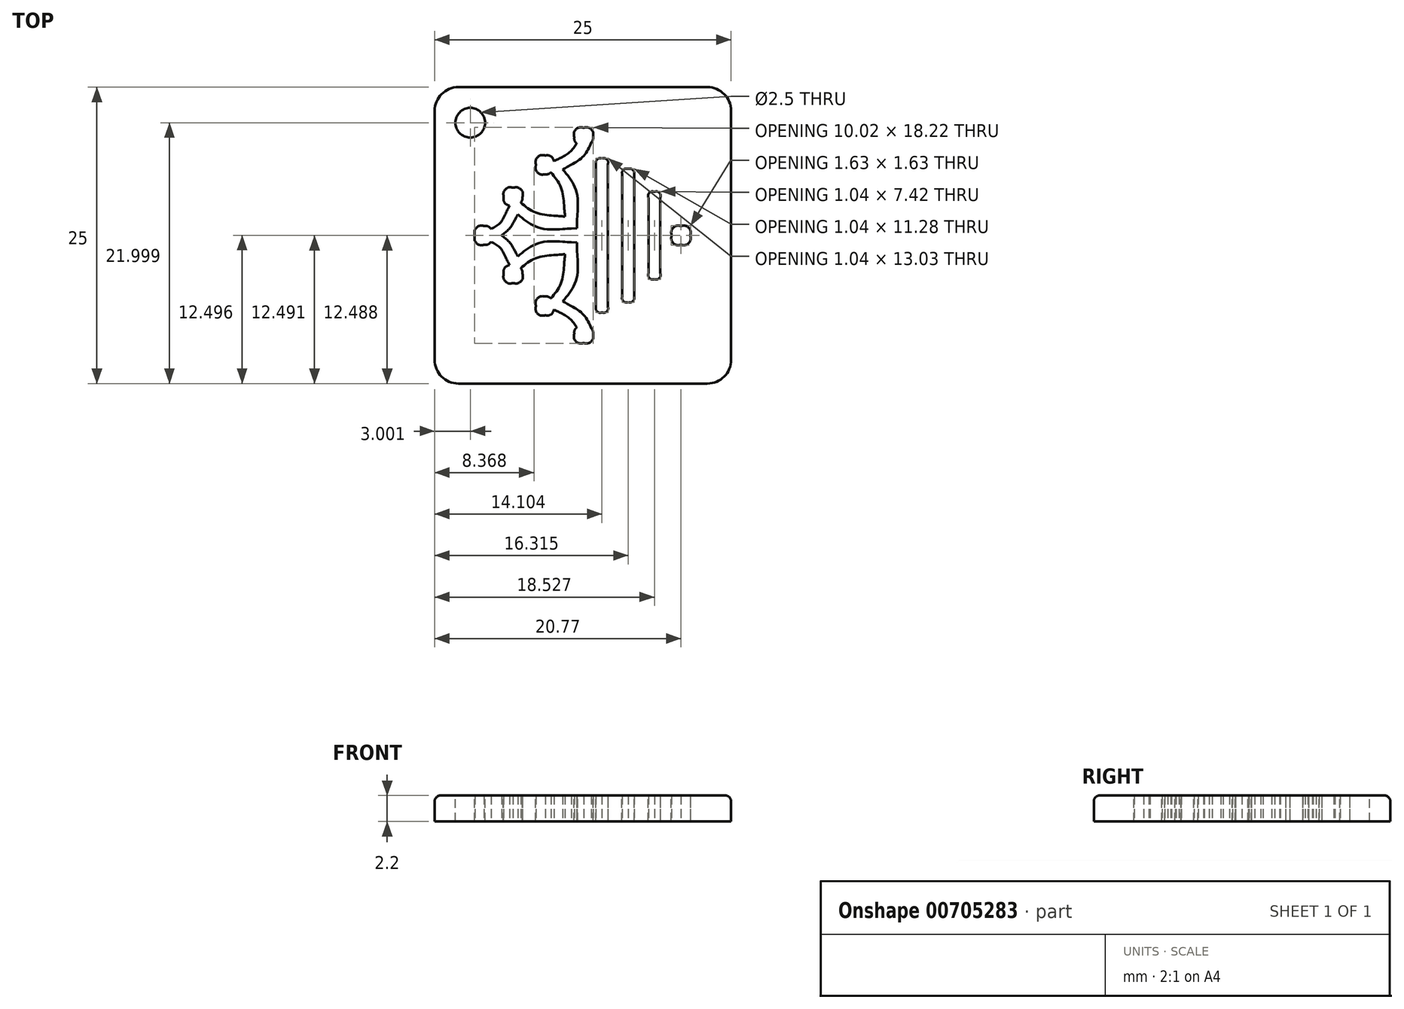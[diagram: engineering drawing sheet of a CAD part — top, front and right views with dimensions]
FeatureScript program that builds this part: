
annotation { "Feature Type Name" : "Feature", "Feature Type Description" : "" }
export const myFeature = defineFeature(function(context is Context, id is Id, definition is map)
    precondition{}
    {
        {
            var Q0;
            Q0=qCreatedBy(makeId("Top.planeOp"),FACE);
            var sketch = newSketch(context, id + "F0", { "sketchPlane" : qUnion([Q0])});
            skLineSegment(sketch, "E0", {"start": v(-141.73, -141.73) * mm, "end": v(141.73, -141.73) * mm});
            skLineSegment(sketch, "E1", {"start": v(141.73, -141.73) * mm, "end": v(141.73, 141.73) * mm});
            skLineSegment(sketch, "E2", {"start": v(141.73, 141.73) * mm, "end": v(-141.73, 141.73) * mm});
            skLineSegment(sketch, "E3", {"start": v(-141.73, 141.73) * mm, "end": v(-141.73, -141.73) * mm});
            skFitSpline(sketch, "E4", {"points": [v(18.18, 73.55) * mm, v(15.03, 73.55) * mm, v(12.48, 71) * mm, v(12.48, 67.84) * mm]});
            skLineSegment(sketch, "E5", {"start": v(12.48, 67.84) * mm, "end": v(12.48, -68.12) * mm});
            skFitSpline(sketch, "E6", {"points": [v(12.48, -68.12) * mm, v(12.48, -71.27) * mm, v(15.03, -73.82) * mm, v(18.18, -73.82) * mm]});
            skFitSpline(sketch, "E7", {"points": [v(18.18, -73.82) * mm, v(21.33, -73.82) * mm, v(23.89, -71.27) * mm, v(23.89, -68.12) * mm]});
            skLineSegment(sketch, "E8", {"start": v(23.89, -68.12) * mm, "end": v(23.89, 67.84) * mm});
            skFitSpline(sketch, "E9", {"points": [v(23.89, 67.84) * mm, v(23.89, 71) * mm, v(21.33, 73.55) * mm, v(18.18, 73.55) * mm]});
            skFitSpline(sketch, "E10", {"points": [v(43.26, 63.62) * mm, v(40.1, 63.62) * mm, v(37.56, 61.06) * mm, v(37.56, 57.91) * mm]});
            skLineSegment(sketch, "E11", {"start": v(37.56, 57.91) * mm, "end": v(37.56, -58.2) * mm});
            skFitSpline(sketch, "E12", {"points": [v(37.56, -58.2) * mm, v(37.56, -61.34) * mm, v(40.1, -63.9) * mm, v(43.26, -63.9) * mm]});
            skFitSpline(sketch, "E13", {"points": [v(43.26, -63.9) * mm, v(46.4, -63.9) * mm, v(48.96, -61.34) * mm, v(48.96, -58.2) * mm]});
            skLineSegment(sketch, "E14", {"start": v(48.96, -58.2) * mm, "end": v(48.96, 57.91) * mm});
            skFitSpline(sketch, "E15", {"points": [v(48.96, 57.91) * mm, v(48.96, 61.06) * mm, v(46.4, 63.62) * mm, v(43.26, 63.62) * mm]});
            skFitSpline(sketch, "E16", {"points": [v(68.34, 41.76) * mm, v(65.19, 41.76) * mm, v(62.63, 39.2) * mm, v(62.63, 36.05) * mm]});
            skLineSegment(sketch, "E17", {"start": v(62.63, 36.05) * mm, "end": v(62.63, -36.26) * mm});
            skFitSpline(sketch, "E18", {"points": [v(62.63, -36.26) * mm, v(62.63, -39.41) * mm, v(65.19, -41.97) * mm, v(68.34, -41.97) * mm]});
            skFitSpline(sketch, "E19", {"points": [v(68.34, -41.97) * mm, v(71.49, -41.97) * mm, v(74.04, -39.41) * mm, v(74.04, -36.26) * mm]});
            skLineSegment(sketch, "E20", {"start": v(74.04, -36.26) * mm, "end": v(74.04, 36.05) * mm});
            skFitSpline(sketch, "E21", {"points": [v(74.04, 36.05) * mm, v(74.04, 39.2) * mm, v(71.49, 41.76) * mm, v(68.34, 41.76) * mm]});
            skFitSpline(sketch, "E22", {"points": [v(93.78, 8.93) * mm, v(88.82, 8.93) * mm, v(84.8, 4.9) * mm, v(84.8, -0.05) * mm]});
            skFitSpline(sketch, "E23", {"points": [v(84.8, -0.05) * mm, v(84.8, -5) * mm, v(88.82, -9.03) * mm, v(93.78, -9.03) * mm]});
            skFitSpline(sketch, "E24", {"points": [v(93.78, -9.03) * mm, v(98.73, -9.03) * mm, v(102.75, -5) * mm, v(102.75, -0.05) * mm]});
            skFitSpline(sketch, "E25", {"points": [v(102.75, -0.05) * mm, v(102.75, 4.9) * mm, v(98.73, 8.93) * mm, v(93.78, 8.93) * mm]});
            skFitSpline(sketch, "E26", {"points": [v(7.97, 88.74) * mm, v(9.03, 90.21) * mm, v(9.66, 92.01) * mm, v(9.66, 93.97) * mm]});
            skFitSpline(sketch, "E27", {"points": [v(9.66, 93.97) * mm, v(9.66, 98.92) * mm, v(5.64, 102.94) * mm, v(0.69, 102.94) * mm]});
            skFitSpline(sketch, "E28", {"points": [v(0.69, 102.94) * mm, v(-4.27, 102.94) * mm, v(-8.28, 98.92) * mm, v(-8.28, 93.97) * mm]});
            skFitSpline(sketch, "E29", {"points": [v(-8.28, 93.97) * mm, v(-8.28, 91.64) * mm, v(-7.4, 89.54) * mm, v(-5.95, 87.94) * mm]});
            skFitSpline(sketch, "E30", {"points": [v(-5.95, 87.94) * mm, v(-13.68, 78.6) * mm, v(-23.82, 72.91) * mm, v(-27.73, 70.94) * mm]});
            skFitSpline(sketch, "E31", {"points": [v(-27.73, 70.94) * mm, v(-29.1, 74.14) * mm, v(-32.28, 76.38) * mm, v(-35.98, 76.38) * mm]});
            skFitSpline(sketch, "E32", {"points": [v(-35.98, 76.38) * mm, v(-40.93, 76.38) * mm, v(-44.95, 72.36) * mm, v(-44.95, 67.4) * mm]});
            skFitSpline(sketch, "E33", {"points": [v(-44.95, 67.4) * mm, v(-44.95, 62.44) * mm, v(-40.93, 58.42) * mm, v(-35.98, 58.42) * mm]});
            skFitSpline(sketch, "E34", {"points": [v(-35.98, 58.42) * mm, v(-33.95, 58.42) * mm, v(-32.09, 59.1) * mm, v(-30.58, 60.24) * mm]});
            skFitSpline(sketch, "E35", {"points": [v(-30.58, 60.24) * mm, v(-20.67, 44.96) * mm, v(-17.87, 26.91) * mm, v(-17.08, 17.88) * mm]});
            skFitSpline(sketch, "E36", {"points": [v(-17.08, 17.88) * mm, v(-26.13, 18.65) * mm, v(-44.2, 21.44) * mm, v(-59.47, 31.37) * mm]});
            skFitSpline(sketch, "E37", {"points": [v(-59.47, 31.37) * mm, v(-58.4, 32.85) * mm, v(-57.76, 34.66) * mm, v(-57.76, 36.63) * mm]});
            skFitSpline(sketch, "E38", {"points": [v(-57.76, 36.63) * mm, v(-57.76, 41.6) * mm, v(-61.77, 45.61) * mm, v(-66.73, 45.61) * mm]});
            skFitSpline(sketch, "E39", {"points": [v(-66.73, 45.61) * mm, v(-71.68, 45.61) * mm, v(-75.7, 41.6) * mm, v(-75.7, 36.63) * mm]});
            skFitSpline(sketch, "E40", {"points": [v(-75.7, 36.63) * mm, v(-75.7, 32.9) * mm, v(-73.43, 29.71) * mm, v(-70.2, 28.35) * mm]});
            skFitSpline(sketch, "E41", {"points": [v(-70.2, 28.35) * mm, v(-72.44, 23.85) * mm, v(-78.89, 12.16) * mm, v(-87.87, 6.09) * mm]});
            skFitSpline(sketch, "E42", {"points": [v(-87.87, 6.09) * mm, v(-89.5, 7.83) * mm, v(-91.82, 8.93) * mm, v(-94.4, 8.93) * mm]});
            skFitSpline(sketch, "E43", {"points": [v(-94.4, 8.93) * mm, v(-99.36, 8.93) * mm, v(-103.38, 4.9) * mm, v(-103.38, -0.05) * mm]});
            skFitSpline(sketch, "E44", {"points": [v(-103.38, -0.05) * mm, v(-103.38, -5) * mm, v(-99.36, -9.03) * mm, v(-94.4, -9.03) * mm]});
            skFitSpline(sketch, "E45", {"points": [v(-94.4, -9.03) * mm, v(-91.82, -9.03) * mm, v(-89.49, -7.92) * mm, v(-87.85, -6.17) * mm]});
            skFitSpline(sketch, "E46", {"points": [v(-87.85, -6.17) * mm, v(-78.88, -12.25) * mm, v(-72.44, -23.95) * mm, v(-70.2, -28.45) * mm]});
            skFitSpline(sketch, "E47", {"points": [v(-70.2, -28.45) * mm, v(-73.43, -29.8) * mm, v(-75.7, -33) * mm, v(-75.7, -36.73) * mm]});
            skFitSpline(sketch, "E48", {"points": [v(-75.7, -36.73) * mm, v(-75.7, -41.69) * mm, v(-71.68, -45.7) * mm, v(-66.73, -45.7) * mm]});
            skFitSpline(sketch, "E49", {"points": [v(-66.73, -45.7) * mm, v(-61.77, -45.7) * mm, v(-57.76, -41.69) * mm, v(-57.76, -36.73) * mm]});
            skFitSpline(sketch, "E50", {"points": [v(-57.76, -36.73) * mm, v(-57.76, -34.76) * mm, v(-58.4, -32.95) * mm, v(-59.47, -31.47) * mm]});
            skFitSpline(sketch, "E51", {"points": [v(-59.47, -31.47) * mm, v(-44.2, -21.53) * mm, v(-26.11, -18.75) * mm, v(-17.07, -17.97) * mm]});
            skFitSpline(sketch, "E52", {"points": [v(-17.07, -17.97) * mm, v(-17.85, -27) * mm, v(-20.63, -45) * mm, v(-30.58, -60.34) * mm]});
            skFitSpline(sketch, "E53", {"points": [v(-30.58, -60.34) * mm, v(-32.09, -59.2) * mm, v(-33.95, -58.52) * mm, v(-35.98, -58.52) * mm]});
            skFitSpline(sketch, "E54", {"points": [v(-35.98, -58.52) * mm, v(-40.93, -58.52) * mm, v(-44.95, -62.54) * mm, v(-44.95, -67.5) * mm]});
            skFitSpline(sketch, "E55", {"points": [v(-44.95, -67.5) * mm, v(-44.95, -72.45) * mm, v(-40.93, -76.47) * mm, v(-35.98, -76.47) * mm]});
            skFitSpline(sketch, "E56", {"points": [v(-35.98, -76.47) * mm, v(-32.28, -76.47) * mm, v(-29.1, -74.23) * mm, v(-27.73, -71.03) * mm]});
            skFitSpline(sketch, "E57", {"points": [v(-27.73, -71.03) * mm, v(-23.81, -72.99) * mm, v(-13.69, -78.64) * mm, v(-5.95, -88.03) * mm]});
            skFitSpline(sketch, "E58", {"points": [v(-5.95, -88.03) * mm, v(-7.4, -89.63) * mm, v(-8.28, -91.74) * mm, v(-8.28, -94.06) * mm]});
            skFitSpline(sketch, "E59", {"points": [v(-8.28, -94.06) * mm, v(-8.28, -99.02) * mm, v(-4.27, -103.04) * mm, v(0.69, -103.04) * mm]});
            skFitSpline(sketch, "E60", {"points": [v(0.69, -103.04) * mm, v(5.64, -103.04) * mm, v(9.66, -99.02) * mm, v(9.66, -94.06) * mm]});
            skFitSpline(sketch, "E61", {"points": [v(9.66, -94.06) * mm, v(9.66, -92.11) * mm, v(9.03, -90.31) * mm, v(7.97, -88.84) * mm]});
            skFitSpline(sketch, "E62", {"points": [v(7.97, -88.84) * mm, v(0.27, -75.6) * mm, v(-12.12, -67.14) * mm, v(-19.34, -63.05) * mm]});
            skFitSpline(sketch, "E63", {"points": [v(-19.34, -63.05) * mm, v(-5.74, -39.72) * mm, v(-5.77, -13.33) * mm, v(-5.78, -12.13) * mm]});
            skLineSegment(sketch, "E64", {"start": v(-5.78, -12.13) * mm, "end": v(-5.82, -6.73) * mm});
            skLineSegment(sketch, "E65", {"start": v(-5.82, -6.73) * mm, "end": v(-11.23, -6.68) * mm});
            skFitSpline(sketch, "E66", {"points": [v(-11.23, -6.68) * mm, v(-12.42, -6.66) * mm, v(-38.8, -6.6) * mm, v(-62.12, -20.18) * mm]});
            skFitSpline(sketch, "E67", {"points": [v(-62.12, -20.18) * mm, v(-65.16, -14.68) * mm, v(-70.52, -6.3) * mm, v(-77.82, -0.04) * mm]});
            skFitSpline(sketch, "E68", {"points": [v(-77.82, -0.04) * mm, v(-70.53, 6.22) * mm, v(-65.16, 14.6) * mm, v(-62.12, 20.09) * mm]});
            skFitSpline(sketch, "E69", {"points": [v(-62.12, 20.09) * mm, v(-38.81, 6.5) * mm, v(-12.43, 6.56) * mm, v(-11.23, 6.58) * mm]});
            skLineSegment(sketch, "E70", {"start": v(-11.23, 6.58) * mm, "end": v(-5.82, 6.63) * mm});
            skLineSegment(sketch, "E71", {"start": v(-5.82, 6.63) * mm, "end": v(-5.78, 12.04) * mm});
            skFitSpline(sketch, "E72", {"points": [v(-5.78, 12.04) * mm, v(-5.77, 13.23) * mm, v(-5.75, 39.63) * mm, v(-19.34, 62.95) * mm]});
            skFitSpline(sketch, "E73", {"points": [v(-19.34, 62.95) * mm, v(-12.12, 67.04) * mm, v(0.27, 75.5) * mm, v(7.97, 88.74) * mm]});
            skSolve(sketch);
        }
        {
            var Q0;
            Q0=makeQuery(id+"F0.imprint","IMPRINT",FACE,{"disambiguationData":[TD([[makeQuery(id+"F0.imprint","IMPRINT",EDGE,{"derivedFrom":sQuery(id+"F0.wireOp",EDGE,"E0")}),1.0]])]});
            extrude(context, id + "F1", {"entities" : qUnion([Q0]), "depth" : 25 * mm, "offsetDistance" : 25 * mm});
        }
        {
            var Q0;
            Q0=makeQuery(id+"F1.opExtrude","SWEPT_BODY",BODY,{"disambiguationData":[OSD([sQuery(id+"F0.wireOp",EDGE,"E0"),sQuery(id+"F0.wireOp",EDGE,"E1"),sQuery(id+"F0.wireOp",EDGE,"E2"),sQuery(id+"F0.wireOp",EDGE,"E3"),sQuery(id+"F0.wireOp",EDGE,"E4"),sQuery(id+"F0.wireOp",EDGE,"E5"),sQuery(id+"F0.wireOp",EDGE,"E6"),sQuery(id+"F0.wireOp",EDGE,"E7"),sQuery(id+"F0.wireOp",EDGE,"E8"),sQuery(id+"F0.wireOp",EDGE,"E9"),sQuery(id+"F0.wireOp",EDGE,"E10"),sQuery(id+"F0.wireOp",EDGE,"E11"),sQuery(id+"F0.wireOp",EDGE,"E12"),sQuery(id+"F0.wireOp",EDGE,"E13"),sQuery(id+"F0.wireOp",EDGE,"E14"),sQuery(id+"F0.wireOp",EDGE,"E15"),sQuery(id+"F0.wireOp",EDGE,"E16"),sQuery(id+"F0.wireOp",EDGE,"E17"),sQuery(id+"F0.wireOp",EDGE,"E18"),sQuery(id+"F0.wireOp",EDGE,"E19"),sQuery(id+"F0.wireOp",EDGE,"E20"),sQuery(id+"F0.wireOp",EDGE,"E21"),sQuery(id+"F0.wireOp",EDGE,"E22"),sQuery(id+"F0.wireOp",EDGE,"E23"),sQuery(id+"F0.wireOp",EDGE,"E24"),sQuery(id+"F0.wireOp",EDGE,"E25"),sQuery(id+"F0.wireOp",EDGE,"E26"),sQuery(id+"F0.wireOp",EDGE,"E27"),sQuery(id+"F0.wireOp",EDGE,"E28"),sQuery(id+"F0.wireOp",EDGE,"E29"),sQuery(id+"F0.wireOp",EDGE,"E30"),sQuery(id+"F0.wireOp",EDGE,"E31"),sQuery(id+"F0.wireOp",EDGE,"E32"),sQuery(id+"F0.wireOp",EDGE,"E33"),sQuery(id+"F0.wireOp",EDGE,"E34"),sQuery(id+"F0.wireOp",EDGE,"E35"),sQuery(id+"F0.wireOp",EDGE,"E36"),sQuery(id+"F0.wireOp",EDGE,"E37"),sQuery(id+"F0.wireOp",EDGE,"E38"),sQuery(id+"F0.wireOp",EDGE,"E39"),sQuery(id+"F0.wireOp",EDGE,"E40"),sQuery(id+"F0.wireOp",EDGE,"E41"),sQuery(id+"F0.wireOp",EDGE,"E42"),sQuery(id+"F0.wireOp",EDGE,"E43"),sQuery(id+"F0.wireOp",EDGE,"E44"),sQuery(id+"F0.wireOp",EDGE,"E45"),sQuery(id+"F0.wireOp",EDGE,"E46"),sQuery(id+"F0.wireOp",EDGE,"E47"),sQuery(id+"F0.wireOp",EDGE,"E48"),sQuery(id+"F0.wireOp",EDGE,"E49"),sQuery(id+"F0.wireOp",EDGE,"E50"),sQuery(id+"F0.wireOp",EDGE,"E51"),sQuery(id+"F0.wireOp",EDGE,"E52"),sQuery(id+"F0.wireOp",EDGE,"E53"),sQuery(id+"F0.wireOp",EDGE,"E54"),sQuery(id+"F0.wireOp",EDGE,"E55"),sQuery(id+"F0.wireOp",EDGE,"E56"),sQuery(id+"F0.wireOp",EDGE,"E57"),sQuery(id+"F0.wireOp",EDGE,"E58"),sQuery(id+"F0.wireOp",EDGE,"E59"),sQuery(id+"F0.wireOp",EDGE,"E60"),sQuery(id+"F0.wireOp",EDGE,"E61"),sQuery(id+"F0.wireOp",EDGE,"E62"),sQuery(id+"F0.wireOp",EDGE,"E63"),sQuery(id+"F0.wireOp",EDGE,"E64"),sQuery(id+"F0.wireOp",EDGE,"E65"),sQuery(id+"F0.wireOp",EDGE,"E66"),sQuery(id+"F0.wireOp",EDGE,"E67"),sQuery(id+"F0.wireOp",EDGE,"E68"),sQuery(id+"F0.wireOp",EDGE,"E69"),sQuery(id+"F0.wireOp",EDGE,"E70"),sQuery(id+"F0.wireOp",EDGE,"E71"),sQuery(id+"F0.wireOp",EDGE,"E72"),sQuery(id+"F0.wireOp",EDGE,"E73")])]});
            var Q1;
            Q1=qCreatedBy(makeId("Origin.pointOp"),VERTEX);
            transform(context, id + "F2", {"entities" : qUnion([Q0]), "transformType" : TransformType.SCALE_UNIFORMLY, "scale" : 0.35 / 4, "scalePoint" : qUnion([Q1]), "makeCopy" : false});
        }
        {
            var Q0;
            Q0=makeQuery(id+"F1.opExtrude","CAP_FACE",FACE,{"disambiguationData":[OSD([sQuery(id+"F0.wireOp",EDGE,"E0"),sQuery(id+"F0.wireOp",EDGE,"E1"),sQuery(id+"F0.wireOp",EDGE,"E2"),sQuery(id+"F0.wireOp",EDGE,"E3"),sQuery(id+"F0.wireOp",EDGE,"E4"),sQuery(id+"F0.wireOp",EDGE,"E5"),sQuery(id+"F0.wireOp",EDGE,"E6"),sQuery(id+"F0.wireOp",EDGE,"E7"),sQuery(id+"F0.wireOp",EDGE,"E8"),sQuery(id+"F0.wireOp",EDGE,"E9"),sQuery(id+"F0.wireOp",EDGE,"E10"),sQuery(id+"F0.wireOp",EDGE,"E11"),sQuery(id+"F0.wireOp",EDGE,"E12"),sQuery(id+"F0.wireOp",EDGE,"E13"),sQuery(id+"F0.wireOp",EDGE,"E14"),sQuery(id+"F0.wireOp",EDGE,"E15"),sQuery(id+"F0.wireOp",EDGE,"E16"),sQuery(id+"F0.wireOp",EDGE,"E17"),sQuery(id+"F0.wireOp",EDGE,"E18"),sQuery(id+"F0.wireOp",EDGE,"E19"),sQuery(id+"F0.wireOp",EDGE,"E20"),sQuery(id+"F0.wireOp",EDGE,"E21"),sQuery(id+"F0.wireOp",EDGE,"E22"),sQuery(id+"F0.wireOp",EDGE,"E23"),sQuery(id+"F0.wireOp",EDGE,"E24"),sQuery(id+"F0.wireOp",EDGE,"E25"),sQuery(id+"F0.wireOp",EDGE,"E26"),sQuery(id+"F0.wireOp",EDGE,"E27"),sQuery(id+"F0.wireOp",EDGE,"E28"),sQuery(id+"F0.wireOp",EDGE,"E29"),sQuery(id+"F0.wireOp",EDGE,"E30"),sQuery(id+"F0.wireOp",EDGE,"E31"),sQuery(id+"F0.wireOp",EDGE,"E32"),sQuery(id+"F0.wireOp",EDGE,"E33"),sQuery(id+"F0.wireOp",EDGE,"E34"),sQuery(id+"F0.wireOp",EDGE,"E35"),sQuery(id+"F0.wireOp",EDGE,"E36"),sQuery(id+"F0.wireOp",EDGE,"E37"),sQuery(id+"F0.wireOp",EDGE,"E38"),sQuery(id+"F0.wireOp",EDGE,"E39"),sQuery(id+"F0.wireOp",EDGE,"E40"),sQuery(id+"F0.wireOp",EDGE,"E41"),sQuery(id+"F0.wireOp",EDGE,"E42"),sQuery(id+"F0.wireOp",EDGE,"E43"),sQuery(id+"F0.wireOp",EDGE,"E44"),sQuery(id+"F0.wireOp",EDGE,"E45"),sQuery(id+"F0.wireOp",EDGE,"E46"),sQuery(id+"F0.wireOp",EDGE,"E47"),sQuery(id+"F0.wireOp",EDGE,"E48"),sQuery(id+"F0.wireOp",EDGE,"E49"),sQuery(id+"F0.wireOp",EDGE,"E50"),sQuery(id+"F0.wireOp",EDGE,"E51"),sQuery(id+"F0.wireOp",EDGE,"E52"),sQuery(id+"F0.wireOp",EDGE,"E53"),sQuery(id+"F0.wireOp",EDGE,"E54"),sQuery(id+"F0.wireOp",EDGE,"E55"),sQuery(id+"F0.wireOp",EDGE,"E56"),sQuery(id+"F0.wireOp",EDGE,"E57"),sQuery(id+"F0.wireOp",EDGE,"E58"),sQuery(id+"F0.wireOp",EDGE,"E59"),sQuery(id+"F0.wireOp",EDGE,"E60"),sQuery(id+"F0.wireOp",EDGE,"E61"),sQuery(id+"F0.wireOp",EDGE,"E62"),sQuery(id+"F0.wireOp",EDGE,"E63"),sQuery(id+"F0.wireOp",EDGE,"E64"),sQuery(id+"F0.wireOp",EDGE,"E65"),sQuery(id+"F0.wireOp",EDGE,"E66"),sQuery(id+"F0.wireOp",EDGE,"E67"),sQuery(id+"F0.wireOp",EDGE,"E68"),sQuery(id+"F0.wireOp",EDGE,"E69"),sQuery(id+"F0.wireOp",EDGE,"E70"),sQuery(id+"F0.wireOp",EDGE,"E71"),sQuery(id+"F0.wireOp",EDGE,"E72"),sQuery(id+"F0.wireOp",EDGE,"E73")])],"isStart":false});
            var sketch = newSketch(context, id + "F3", { "sketchPlane" : qUnion([Q0])});
            skLineSegment(sketch, "E74.0", {"start": v(12.5, 9.5) * mm, "end": v(-12.5, 9.5) * mm, "construction": true});
            skLineSegment(sketch, "E75.0", {"start": v(-9.5, 12.5) * mm, "end": v(-9.5, -12.5) * mm, "construction": true});
            skCircle(sketch, "E76", {"center": v(-9.5, 9.5) * mm, "radius": 1.33 * mm, "construction": true});
            skSolve(sketch);
        }
        {
            var Q0;
            Q0=sQuery(id+"F3.wireOp",VERTEX,"E76.center");
            var Q1;
            Q1=makeQuery(id+"F1.opExtrude","SWEPT_BODY",BODY,{"disambiguationData":[OSD([sQuery(id+"F0.wireOp",EDGE,"E0"),sQuery(id+"F0.wireOp",EDGE,"E1"),sQuery(id+"F0.wireOp",EDGE,"E2"),sQuery(id+"F0.wireOp",EDGE,"E3"),sQuery(id+"F0.wireOp",EDGE,"E4"),sQuery(id+"F0.wireOp",EDGE,"E5"),sQuery(id+"F0.wireOp",EDGE,"E6"),sQuery(id+"F0.wireOp",EDGE,"E7"),sQuery(id+"F0.wireOp",EDGE,"E8"),sQuery(id+"F0.wireOp",EDGE,"E9"),sQuery(id+"F0.wireOp",EDGE,"E10"),sQuery(id+"F0.wireOp",EDGE,"E11"),sQuery(id+"F0.wireOp",EDGE,"E12"),sQuery(id+"F0.wireOp",EDGE,"E13"),sQuery(id+"F0.wireOp",EDGE,"E14"),sQuery(id+"F0.wireOp",EDGE,"E15"),sQuery(id+"F0.wireOp",EDGE,"E16"),sQuery(id+"F0.wireOp",EDGE,"E17"),sQuery(id+"F0.wireOp",EDGE,"E18"),sQuery(id+"F0.wireOp",EDGE,"E19"),sQuery(id+"F0.wireOp",EDGE,"E20"),sQuery(id+"F0.wireOp",EDGE,"E21"),sQuery(id+"F0.wireOp",EDGE,"E22"),sQuery(id+"F0.wireOp",EDGE,"E23"),sQuery(id+"F0.wireOp",EDGE,"E24"),sQuery(id+"F0.wireOp",EDGE,"E25"),sQuery(id+"F0.wireOp",EDGE,"E26"),sQuery(id+"F0.wireOp",EDGE,"E27"),sQuery(id+"F0.wireOp",EDGE,"E28"),sQuery(id+"F0.wireOp",EDGE,"E29"),sQuery(id+"F0.wireOp",EDGE,"E30"),sQuery(id+"F0.wireOp",EDGE,"E31"),sQuery(id+"F0.wireOp",EDGE,"E32"),sQuery(id+"F0.wireOp",EDGE,"E33"),sQuery(id+"F0.wireOp",EDGE,"E34"),sQuery(id+"F0.wireOp",EDGE,"E35"),sQuery(id+"F0.wireOp",EDGE,"E36"),sQuery(id+"F0.wireOp",EDGE,"E37"),sQuery(id+"F0.wireOp",EDGE,"E38"),sQuery(id+"F0.wireOp",EDGE,"E39"),sQuery(id+"F0.wireOp",EDGE,"E40"),sQuery(id+"F0.wireOp",EDGE,"E41"),sQuery(id+"F0.wireOp",EDGE,"E42"),sQuery(id+"F0.wireOp",EDGE,"E43"),sQuery(id+"F0.wireOp",EDGE,"E44"),sQuery(id+"F0.wireOp",EDGE,"E45"),sQuery(id+"F0.wireOp",EDGE,"E46"),sQuery(id+"F0.wireOp",EDGE,"E47"),sQuery(id+"F0.wireOp",EDGE,"E48"),sQuery(id+"F0.wireOp",EDGE,"E49"),sQuery(id+"F0.wireOp",EDGE,"E50"),sQuery(id+"F0.wireOp",EDGE,"E51"),sQuery(id+"F0.wireOp",EDGE,"E52"),sQuery(id+"F0.wireOp",EDGE,"E53"),sQuery(id+"F0.wireOp",EDGE,"E54"),sQuery(id+"F0.wireOp",EDGE,"E55"),sQuery(id+"F0.wireOp",EDGE,"E56"),sQuery(id+"F0.wireOp",EDGE,"E57"),sQuery(id+"F0.wireOp",EDGE,"E58"),sQuery(id+"F0.wireOp",EDGE,"E59"),sQuery(id+"F0.wireOp",EDGE,"E60"),sQuery(id+"F0.wireOp",EDGE,"E61"),sQuery(id+"F0.wireOp",EDGE,"E62"),sQuery(id+"F0.wireOp",EDGE,"E63"),sQuery(id+"F0.wireOp",EDGE,"E64"),sQuery(id+"F0.wireOp",EDGE,"E65"),sQuery(id+"F0.wireOp",EDGE,"E66"),sQuery(id+"F0.wireOp",EDGE,"E67"),sQuery(id+"F0.wireOp",EDGE,"E68"),sQuery(id+"F0.wireOp",EDGE,"E69"),sQuery(id+"F0.wireOp",EDGE,"E70"),sQuery(id+"F0.wireOp",EDGE,"E71"),sQuery(id+"F0.wireOp",EDGE,"E72"),sQuery(id+"F0.wireOp",EDGE,"E73")])]});
            hole(context, id + "F4", {"style" : HoleStyle.SIMPLE, "endStyle" : HoleEndStyle.THROUGH, "holeDiameter" : 2.5 * mm, "majorDiameter" : 5 * mm, "isTappedThrough" : true, "tappedDepth" : 12 * mm, "tapClearance" : 3, "locations" : qUnion([Q0]), "scope" : qUnion([Q1])});
        }
        {
            var Q0;
            Q0=makeQuery(id+"F1.opExtrude","SWEPT_EDGE",EDGE,{"disambiguationData":[OSD([sQuery(id+"F0.wireOp",EDGE,"E0"),sQuery(id+"F0.wireOp",EDGE,"E3")])]});
            var Q1;
            Q1=makeQuery(id+"F1.opExtrude","SWEPT_EDGE",EDGE,{"disambiguationData":[OSD([sQuery(id+"F0.wireOp",EDGE,"E2"),sQuery(id+"F0.wireOp",EDGE,"E3")])]});
            var Q2;
            Q2=makeQuery(id+"F1.opExtrude","SWEPT_EDGE",EDGE,{"disambiguationData":[OSD([sQuery(id+"F0.wireOp",EDGE,"E0"),sQuery(id+"F0.wireOp",EDGE,"E1")])]});
            var Q3;
            Q3=makeQuery(id+"F1.opExtrude","SWEPT_EDGE",EDGE,{"disambiguationData":[OSD([sQuery(id+"F0.wireOp",EDGE,"E1"),sQuery(id+"F0.wireOp",EDGE,"E2")])]});
            fillet(context, id + "F5", {"entities" : qUnion([Q0, Q1, Q2, Q3]), "radius" : 2 * mm, "tangentPropagation" : true, "allowEdgeOverflow" : false});
        }
        {
            var Q0;
            Q0=makeQuery(id+"F1.opExtrude","CAP_EDGE",EDGE,{"disambiguationData":[OSD([sQuery(id+"F0.wireOp",EDGE,"E0")])],"isStart":false});
            fillet(context, id + "F6", {"entities" : qUnion([Q0]), "radius" : .5 * mm, "tangentPropagation" : true, "allowEdgeOverflow" : false});
        }
    });
